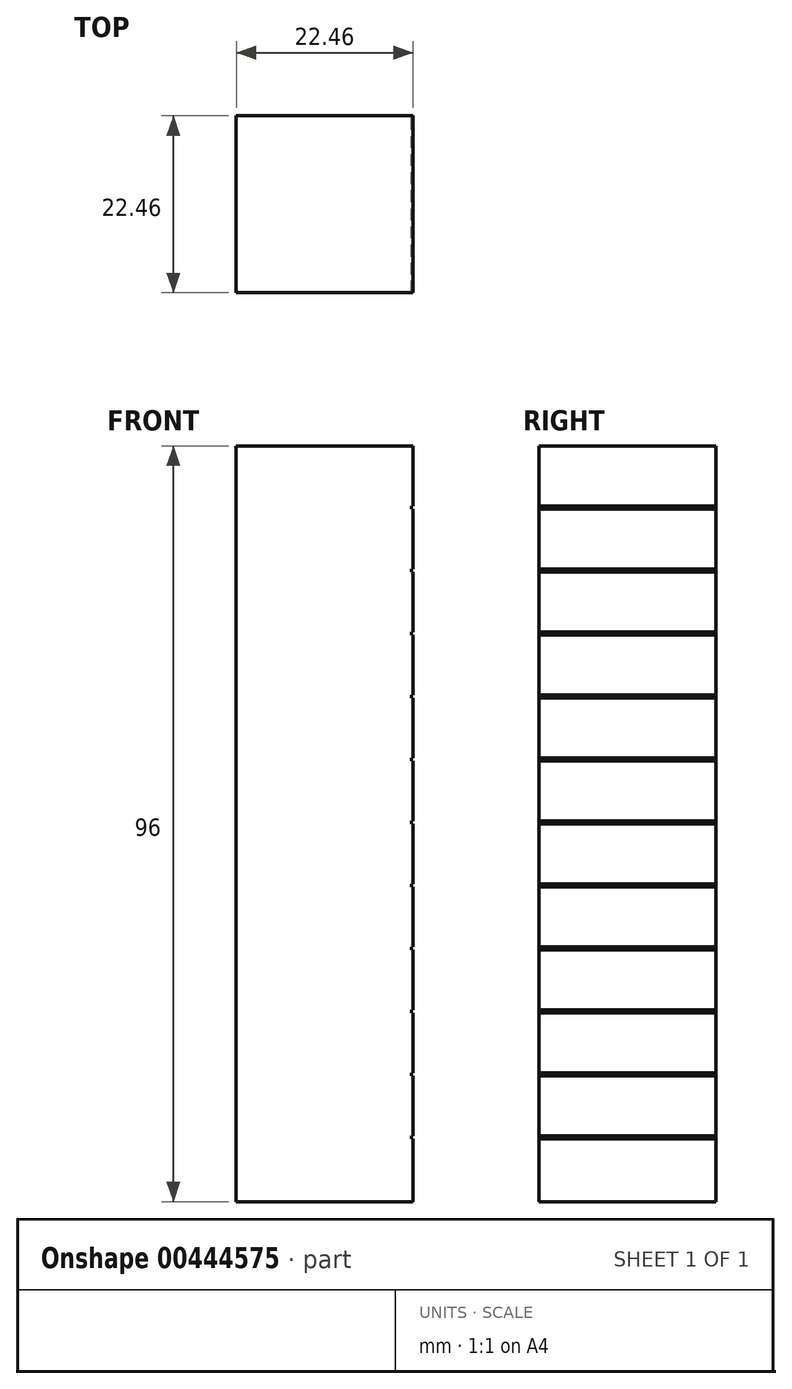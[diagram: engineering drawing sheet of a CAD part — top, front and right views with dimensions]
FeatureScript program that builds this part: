
annotation { "Feature Type Name" : "Feature", "Feature Type Description" : "" }
export const myFeature = defineFeature(function(context is Context, id is Id, definition is map)
    precondition{}
    {
        {
            var Q0;
            Q0=qCreatedBy(makeId("Top.planeOp"),FACE);
            var sketch = newSketch(context, id + "F0", { "sketchPlane" : qUnion([Q0])});
            skLineSegment(sketch, "E0.bottom", {"start": v(11.23, -11.23) * mm, "end": v(-11.23, -11.23) * mm});
            skLineSegment(sketch, "E0.top", {"start": v(11.23, 11.23) * mm, "end": v(-11.23, 11.23) * mm});
            skLineSegment(sketch, "E0.left", {"start": v(11.23, -11.23) * mm, "end": v(11.23, 11.23) * mm});
            skLineSegment(sketch, "E0.right", {"start": v(-11.23, -11.23) * mm, "end": v(-11.23, 11.23) * mm});
            skPoint(sketch, "E0.middle", {"position": v(0, 0) * mm});
            skSolve(sketch);
        }
        {
            var Q0;
            Q0=makeQuery(id+"F0.imprint","IMPRINT",FACE,{"disambiguationData":[TD([[makeQuery(id+"F0.imprint","IMPRINT",EDGE,{"derivedFrom":sQuery(id+"F0.wireOp",EDGE,"E0.bottom")}),-1.0]])]});
            extrude(context, id + "F1", {"entities" : qUnion([Q0]), "depth" : 96 * mm});
        }
        {
            var Q0;
            Q0=makeQuery(id+"F1.opExtrude","SWEPT_FACE",FACE,{"disambiguationData":[OSD([sQuery(id+"F0.wireOp",EDGE,"E0.left")])]});
            var sketch = newSketch(context, id + "F2", { "sketchPlane" : qUnion([Q0])});
            skLineSegment(sketch, "E1.bottom", {"start": v(-11.23, 8) * mm, "end": v(11.23, 8) * mm});
            skLineSegment(sketch, "E1.top", {"start": v(-11.23, 8.4) * mm, "end": v(11.23, 8.4) * mm});
            skLineSegment(sketch, "E1.left", {"start": v(-11.23, 8) * mm, "end": v(-11.23, 8.4) * mm});
            skLineSegment(sketch, "E1.right", {"start": v(11.23, 8) * mm, "end": v(11.23, 8.4) * mm});
            skLineSegment(sketch, "E2.bottom", {"start": v(-11.23, 16) * mm, "end": v(11.23, 16) * mm});
            skLineSegment(sketch, "E2.top", {"start": v(-11.23, 16.4) * mm, "end": v(11.23, 16.4) * mm});
            skLineSegment(sketch, "E2.left", {"start": v(-11.23, 16) * mm, "end": v(-11.23, 16.4) * mm});
            skLineSegment(sketch, "E2.right", {"start": v(11.23, 16) * mm, "end": v(11.23, 16.4) * mm});
            skLineSegment(sketch, "E3.bottom", {"start": v(-11.23, 24) * mm, "end": v(11.23, 24) * mm});
            skLineSegment(sketch, "E3.top", {"start": v(-11.23, 24.4) * mm, "end": v(11.23, 24.4) * mm});
            skLineSegment(sketch, "E3.left", {"start": v(-11.23, 24) * mm, "end": v(-11.23, 24.4) * mm});
            skLineSegment(sketch, "E3.right", {"start": v(11.23, 24) * mm, "end": v(11.23, 24.4) * mm});
            skLineSegment(sketch, "E4.bottom", {"start": v(-11.23, 32.4) * mm, "end": v(11.23, 32.4) * mm});
            skLineSegment(sketch, "E4.top", {"start": v(-11.23, 32) * mm, "end": v(11.23, 32) * mm});
            skLineSegment(sketch, "E4.left", {"start": v(-11.23, 32) * mm, "end": v(-11.23, 32.4) * mm});
            skLineSegment(sketch, "E4.right", {"start": v(11.23, 32) * mm, "end": v(11.23, 32.4) * mm});
            skLineSegment(sketch, "E5.bottom", {"start": v(-11.23, 40) * mm, "end": v(11.23, 40) * mm});
            skLineSegment(sketch, "E5.top", {"start": v(-11.23, 40.4) * mm, "end": v(11.23, 40.4) * mm});
            skLineSegment(sketch, "E5.left", {"start": v(-11.23, 40) * mm, "end": v(-11.23, 40.4) * mm});
            skLineSegment(sketch, "E5.right", {"start": v(11.23, 40) * mm, "end": v(11.23, 40.4) * mm});
            skLineSegment(sketch, "E6.bottom", {"start": v(-11.23, 48) * mm, "end": v(11.23, 48) * mm});
            skLineSegment(sketch, "E6.top", {"start": v(-11.23, 48.4) * mm, "end": v(11.23, 48.4) * mm});
            skLineSegment(sketch, "E6.left", {"start": v(-11.23, 48) * mm, "end": v(-11.23, 48.4) * mm});
            skLineSegment(sketch, "E6.right", {"start": v(11.23, 48) * mm, "end": v(11.23, 48.4) * mm});
            skLineSegment(sketch, "E7.bottom", {"start": v(-11.23, 56) * mm, "end": v(11.23, 56) * mm});
            skLineSegment(sketch, "E7.top", {"start": v(-11.23, 56.4) * mm, "end": v(11.23, 56.4) * mm});
            skLineSegment(sketch, "E7.left", {"start": v(-11.23, 56) * mm, "end": v(-11.23, 56.4) * mm});
            skLineSegment(sketch, "E7.right", {"start": v(11.23, 56) * mm, "end": v(11.23, 56.4) * mm});
            skLineSegment(sketch, "E8.bottom", {"start": v(-11.23, 64) * mm, "end": v(11.23, 64) * mm});
            skLineSegment(sketch, "E8.top", {"start": v(-11.23, 64.4) * mm, "end": v(11.23, 64.4) * mm});
            skLineSegment(sketch, "E8.left", {"start": v(-11.23, 64) * mm, "end": v(-11.23, 64.4) * mm});
            skLineSegment(sketch, "E8.right", {"start": v(11.23, 64) * mm, "end": v(11.23, 64.4) * mm});
            skLineSegment(sketch, "E9.bottom", {"start": v(-11.23, 72) * mm, "end": v(11.23, 72) * mm});
            skLineSegment(sketch, "E9.top", {"start": v(-11.23, 72.4) * mm, "end": v(11.23, 72.4) * mm});
            skLineSegment(sketch, "E9.left", {"start": v(-11.23, 72) * mm, "end": v(-11.23, 72.4) * mm});
            skLineSegment(sketch, "E9.right", {"start": v(11.23, 72) * mm, "end": v(11.23, 72.4) * mm});
            skLineSegment(sketch, "E10.bottom", {"start": v(-11.23, 80.4) * mm, "end": v(11.23, 80.4) * mm});
            skLineSegment(sketch, "E10.top", {"start": v(-11.23, 80) * mm, "end": v(11.23, 80) * mm});
            skLineSegment(sketch, "E10.left", {"start": v(-11.23, 80.4) * mm, "end": v(-11.23, 80) * mm});
            skLineSegment(sketch, "E10.right", {"start": v(11.23, 80.4) * mm, "end": v(11.23, 80) * mm});
            skLineSegment(sketch, "E11.bottom", {"start": v(-11.23, 88.4) * mm, "end": v(11.23, 88.4) * mm});
            skLineSegment(sketch, "E11.top", {"start": v(-11.23, 88) * mm, "end": v(11.23, 88) * mm});
            skLineSegment(sketch, "E11.left", {"start": v(-11.23, 88.4) * mm, "end": v(-11.23, 88) * mm});
            skLineSegment(sketch, "E11.right", {"start": v(11.23, 88.4) * mm, "end": v(11.23, 88) * mm});
            skSolve(sketch);
        }
        {
            var Q0;
            Q0=makeQuery(id+"F2.imprint","IMPRINT",FACE,{"disambiguationData":[TD([[makeQuery(id+"F2.imprint","IMPRINT",EDGE,{"derivedFrom":sQuery(id+"F2.wireOp",EDGE,"E11.bottom")}),-1.0]])]});
            var Q1;
            Q1=makeQuery(id+"F2.imprint","IMPRINT",FACE,{"disambiguationData":[TD([[makeQuery(id+"F2.imprint","IMPRINT",EDGE,{"derivedFrom":sQuery(id+"F2.wireOp",EDGE,"E10.bottom")}),-1.0]])]});
            var Q2;
            Q2=makeQuery(id+"F2.imprint","IMPRINT",FACE,{"disambiguationData":[TD([[makeQuery(id+"F2.imprint","IMPRINT",EDGE,{"derivedFrom":sQuery(id+"F2.wireOp",EDGE,"E9.bottom")}),1.0]])]});
            var Q3;
            Q3=makeQuery(id+"F2.imprint","IMPRINT",FACE,{"disambiguationData":[TD([[makeQuery(id+"F2.imprint","IMPRINT",EDGE,{"derivedFrom":sQuery(id+"F2.wireOp",EDGE,"E8.bottom")}),1.0]])]});
            var Q4;
            Q4=makeQuery(id+"F2.imprint","IMPRINT",FACE,{"disambiguationData":[TD([[makeQuery(id+"F2.imprint","IMPRINT",EDGE,{"derivedFrom":sQuery(id+"F2.wireOp",EDGE,"E7.bottom")}),1.0]])]});
            var Q5;
            Q5=makeQuery(id+"F2.imprint","IMPRINT",FACE,{"disambiguationData":[TD([[makeQuery(id+"F2.imprint","IMPRINT",EDGE,{"derivedFrom":sQuery(id+"F2.wireOp",EDGE,"E6.bottom")}),1.0]])]});
            var Q6;
            Q6=makeQuery(id+"F2.imprint","IMPRINT",FACE,{"disambiguationData":[TD([[makeQuery(id+"F2.imprint","IMPRINT",EDGE,{"derivedFrom":sQuery(id+"F2.wireOp",EDGE,"E5.bottom")}),1.0]])]});
            var Q7;
            Q7=makeQuery(id+"F2.imprint","IMPRINT",FACE,{"disambiguationData":[TD([[makeQuery(id+"F2.imprint","IMPRINT",EDGE,{"derivedFrom":sQuery(id+"F2.wireOp",EDGE,"E4.bottom")}),-1.0]])]});
            var Q8;
            Q8=makeQuery(id+"F2.imprint","IMPRINT",FACE,{"disambiguationData":[TD([[makeQuery(id+"F2.imprint","IMPRINT",EDGE,{"derivedFrom":sQuery(id+"F2.wireOp",EDGE,"E3.bottom")}),1.0]])]});
            var Q9;
            Q9=makeQuery(id+"F2.imprint","IMPRINT",FACE,{"disambiguationData":[TD([[makeQuery(id+"F2.imprint","IMPRINT",EDGE,{"derivedFrom":sQuery(id+"F2.wireOp",EDGE,"E2.bottom")}),1.0]])]});
            var Q10;
            Q10=makeQuery(id+"F2.imprint","IMPRINT",FACE,{"disambiguationData":[TD([[makeQuery(id+"F2.imprint","IMPRINT",EDGE,{"derivedFrom":sQuery(id+"F2.wireOp",EDGE,"E1.bottom")}),1.0]])]});
            extrude(context, id + "F3", {"entities" : qUnion([Q0, Q1, Q2, Q3, Q4, Q5, Q6, Q7, Q8, Q9, Q10]), "operationType" : NewBodyOperationType.REMOVE, "oppositeDirection" : true, "depth" : 0.2 * mm});
        }
    });
